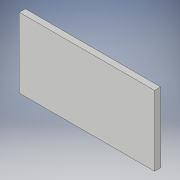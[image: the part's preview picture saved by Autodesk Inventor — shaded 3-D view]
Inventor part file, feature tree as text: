
AUTODESK INVENTOR PART (.ipt)
format: ipt  version: 2017 (Build 210142000, 142)  size: 89,600 bytes
history: native  units: in
note: dims shown in document units (in); Inventor stores cm internally (conversion verified against a paired STEP export)
features: extrude x1, sketch x1
ambient origin geometry x8: Origin, YZ Plane, XZ Plane, XY Plane, X Axis, Y Axis, Z Axis, Center Point
bodies: Solid1 (feature_tree)
feature tree (2):
  extrude  "Extrusion1"  Depth=10.0in
  sketch  "Sketch1"  dims[d0=19.3333in d1=10.0in d2=0.875in d3=0.0in]
